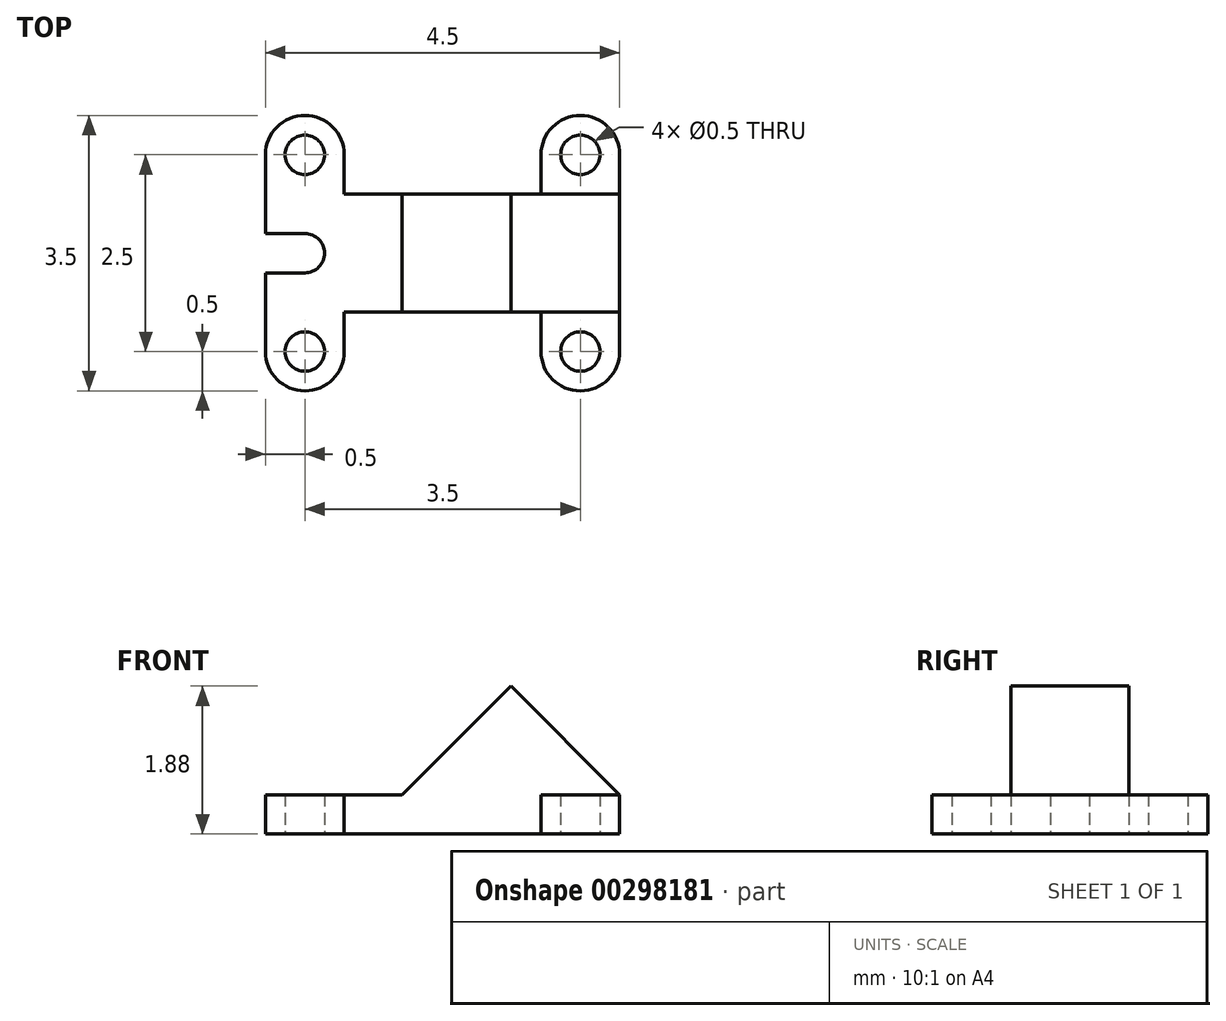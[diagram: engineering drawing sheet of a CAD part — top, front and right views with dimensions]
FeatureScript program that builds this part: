
annotation { "Feature Type Name" : "Feature", "Feature Type Description" : "" }
export const myFeature = defineFeature(function(context is Context, id is Id, definition is map)
    precondition{}
    {
        {
            var Q0;
            Q0=qCreatedBy(makeId("Top.planeOp"),FACE);
            var sketch = newSketch(context, id + "F0", { "sketchPlane" : qUnion([Q0])});
            skCircle(sketch, "E0", {"center": v(0, 0) * mm, "radius": 0.25 * mm});
            skArc(sketch, "E1", {"start": v(-0.5, 0) * mm, "mid": v(0, -0.5) * mm, "end": v(0.5, 0) * mm});
            skCircle(sketch, "E2", {"center": v(0, 2.5) * mm, "radius": 0.25 * mm});
            skArc(sketch, "E3", {"start": v(0.5, 2.5) * mm, "mid": v(0, 3) * mm, "end": v(-0.5, 2.5) * mm});
            skArc(sketch, "E4", {"start": v(0, 1) * mm, "mid": v(0.25, 1.25) * mm, "end": v(0, 1.5) * mm});
            skLineSegment(sketch, "E5", {"start": v(-0.5, 2.5) * mm, "end": v(-0.5, 1.5) * mm});
            skLineSegment(sketch, "E6", {"start": v(-0.5, 0) * mm, "end": v(-0.5, 1) * mm});
            skLineSegment(sketch, "E7", {"start": v(-0.5, 1) * mm, "end": v(0, 1) * mm});
            skLineSegment(sketch, "E8", {"start": v(-0.5, 1.5) * mm, "end": v(0, 1.5) * mm});
            skCircle(sketch, "E9", {"center": v(3.5, 0) * mm, "radius": 0.25 * mm});
            skCircle(sketch, "E10", {"center": v(3.5, 2.5) * mm, "radius": 0.25 * mm});
            skArc(sketch, "E11", {"start": v(4, 2.5) * mm, "mid": v(3.5, 3) * mm, "end": v(3, 2.5) * mm});
            skArc(sketch, "E12", {"start": v(3, 0) * mm, "mid": v(3.5, -0.5) * mm, "end": v(4, 0) * mm});
            skLineSegment(sketch, "E13", {"start": v(4, 2.5) * mm, "end": v(4, 0) * mm});
            skLineSegment(sketch, "E14", {"start": v(0.5, 2.5) * mm, "end": v(0.5, 2) * mm});
            skLineSegment(sketch, "E15", {"start": v(0.5, 0) * mm, "end": v(0.5, 0.5) * mm});
            skLineSegment(sketch, "E16", {"start": v(3, 2.5) * mm, "end": v(3, 2) * mm});
            skLineSegment(sketch, "E17", {"start": v(3, 0) * mm, "end": v(3, 0.5) * mm});
            skLineSegment(sketch, "E18", {"start": v(3, 0.5) * mm, "end": v(0.5, 0.5) * mm});
            skLineSegment(sketch, "E19", {"start": v(0.5, 2) * mm, "end": v(3, 2) * mm});
            skSolve(sketch);
        }
        {
            var Q0;
            Q0 = qSketchRegion(id + "F0", true);
            extrude(context, id + "F1", {"entities" : qUnion([Q0]), "depth" : .5 * mm});
        }
        {
            var Q0;
            Q0=qCreatedBy(makeId("Front.planeOp"),FACE);
            var sketch = newSketch(context, id + "F2", { "sketchPlane" : qUnion([Q0])});
            skLineSegment(sketch, "E20", {"start": v(1.23, 0.5) * mm, "end": v(2.62, 1.88) * mm});
            skLineSegment(sketch, "E21", {"start": v(2.62, 1.88) * mm, "end": v(4, 0.5) * mm});
            skLineSegment(sketch, "E22", {"start": v(1.23, 0.5) * mm, "end": v(4, 0.5) * mm});
            skSolve(sketch);
        }
        {
            var Q0;
            Q0 = qSketchRegion(id + "F2", true);
            extrude(context, id + "F3", {"entities" : qUnion([Q0]), "operationType" : NewBodyOperationType.ADD, "oppositeDirection" : true, "depth" : 2 * mm});
        }
        {
            var Q0;
            Q0=qCreatedBy(makeId("Front.planeOp"),FACE);
            var sketch = newSketch(context, id + "F4", { "sketchPlane" : qUnion([Q0])});
            skLineSegment(sketch, "E23.bottom", {"start": v(4, 2.88) * mm, "end": v(-0.45, 2.88) * mm});
            skLineSegment(sketch, "E23.top", {"start": v(4, 0.5) * mm, "end": v(-0.45, 0.5) * mm});
            skLineSegment(sketch, "E23.left", {"start": v(4, 2.88) * mm, "end": v(4, 0.5) * mm});
            skLineSegment(sketch, "E23.right", {"start": v(-0.45, 2.88) * mm, "end": v(-0.45, 0.5) * mm});
            skSolve(sketch);
        }
        {
            var Q0;
            Q0 = qSketchRegion(id + "F4", true);
            extrude(context, id + "F5", {"entities" : qUnion([Q0]), "operationType" : NewBodyOperationType.REMOVE, "oppositeDirection" : true, "depth" : .5 * mm});
        }
        {
            var Q0;
            Q0=makeQuery(id+"F3.opExtrude","SWEPT_FACE",FACE,{"disambiguationData":[OSD([sQuery(id+"F2.wireOp",EDGE,"E21")])]});
            var sketch = newSketch(context, id + "F6", { "sketchPlane" : qUnion([Q0])});
            skArc(sketch, "E24", {"start": v(1.27, 2) * mm, "mid": v(0.52, 1.25) * mm, "end": v(1.27, 0.5) * mm});
            skLineSegment(sketch, "E25", {"start": v(1.27, 0.5) * mm, "end": v(0.52, 0.5) * mm});
            skLineSegment(sketch, "E26", {"start": v(0.52, 0.5) * mm, "end": v(0.52, 2) * mm});
            skLineSegment(sketch, "E27", {"start": v(0.52, 2) * mm, "end": v(1.27, 2) * mm});
            skSolve(sketch);
        }
        {
            var Q0;
            Q0 = qSketchRegion(id + "F6", true);
            var Q1;
            {var subQ0=sQuery(id+"F0.wireOp",EDGE,"E8");var subQ1=sQuery(id+"F0.wireOp",EDGE,"E7");var subQ2=sQuery(id+"F0.wireOp",EDGE,"E6");var subQ4=sQuery(id+"F0.wireOp",EDGE,"E5");var subQ5=sQuery(id+"F0.wireOp",EDGE,"E4");var subQ7=sQuery(id+"F0.wireOp",EDGE,"E0");var subQ8=sQuery(id+"F0.wireOp",EDGE,"E14");var subQ9=sQuery(id+"F0.wireOp",EDGE,"E3");var subQ10=sQuery(id+"F0.wireOp",EDGE,"E1");var subQ11=sQuery(id+"F0.wireOp",EDGE,"E2");var subQ12=sQuery(id+"F0.wireOp",EDGE,"E15");var subQ13=sQuery(id+"F0.wireOp",EDGE,"E18");var subQ14=sQuery(id+"F0.wireOp",EDGE,"E19");Q1=makeQuery(id+"F3.boolean.opBoolean","SPLIT",FACE,{"disambiguationData":[TD([makeQuery(id+"F1.opExtrude","SWEPT_FACE",FACE,{"disambiguationData":[OSD([subQ7])]})])],"derivedFrom":makeQuery(id+"F1.opExtrude","CAP_FACE",FACE,{"disambiguationData":[OSD([subQ7,subQ10,subQ11,subQ9,subQ5,subQ4,subQ2,subQ1,subQ0,sQuery(id+"F0.wireOp",EDGE,"E9"),sQuery(id+"F0.wireOp",EDGE,"E10"),sQuery(id+"F0.wireOp",EDGE,"E11"),sQuery(id+"F0.wireOp",EDGE,"E12"),sQuery(id+"F0.wireOp",EDGE,"E13"),subQ8,subQ12,sQuery(id+"F0.wireOp",EDGE,"E16"),sQuery(id+"F0.wireOp",EDGE,"E17"),subQ13,subQ14])],"isStart":false})});}
            extrude(context, id + "F7", {"entities" : qUnion([Q0]), "operationType" : NewBodyOperationType.REMOVE, "endBound" : BoundingType.UP_TO_SURFACE, "oppositeDirection" : true, "endBoundEntityFace" : qUnion([Q1]), "depth" : 25 * mm});
        }
        {
            var Q0;
            Q0=makeQuery(id+"F3.opExtrude","SWEPT_FACE",FACE,{"disambiguationData":[OSD([sQuery(id+"F2.wireOp",EDGE,"E21")])]});
            var sketch = newSketch(context, id + "F8", { "sketchPlane" : qUnion([Q0])});
            skCircle(sketch, "E28", {"center": v(1.27, 1.25) * mm, "radius": 0.3 * mm});
            skSolve(sketch);
        }
        {
            var Q0;
            Q0 = qSketchRegion(id + "F8", true);
            extrude(context, id + "F9", {"entities" : qUnion([Q0]), "operationType" : NewBodyOperationType.REMOVE, "oppositeDirection" : true, "depth" : 25 * mm});
        }
    });
